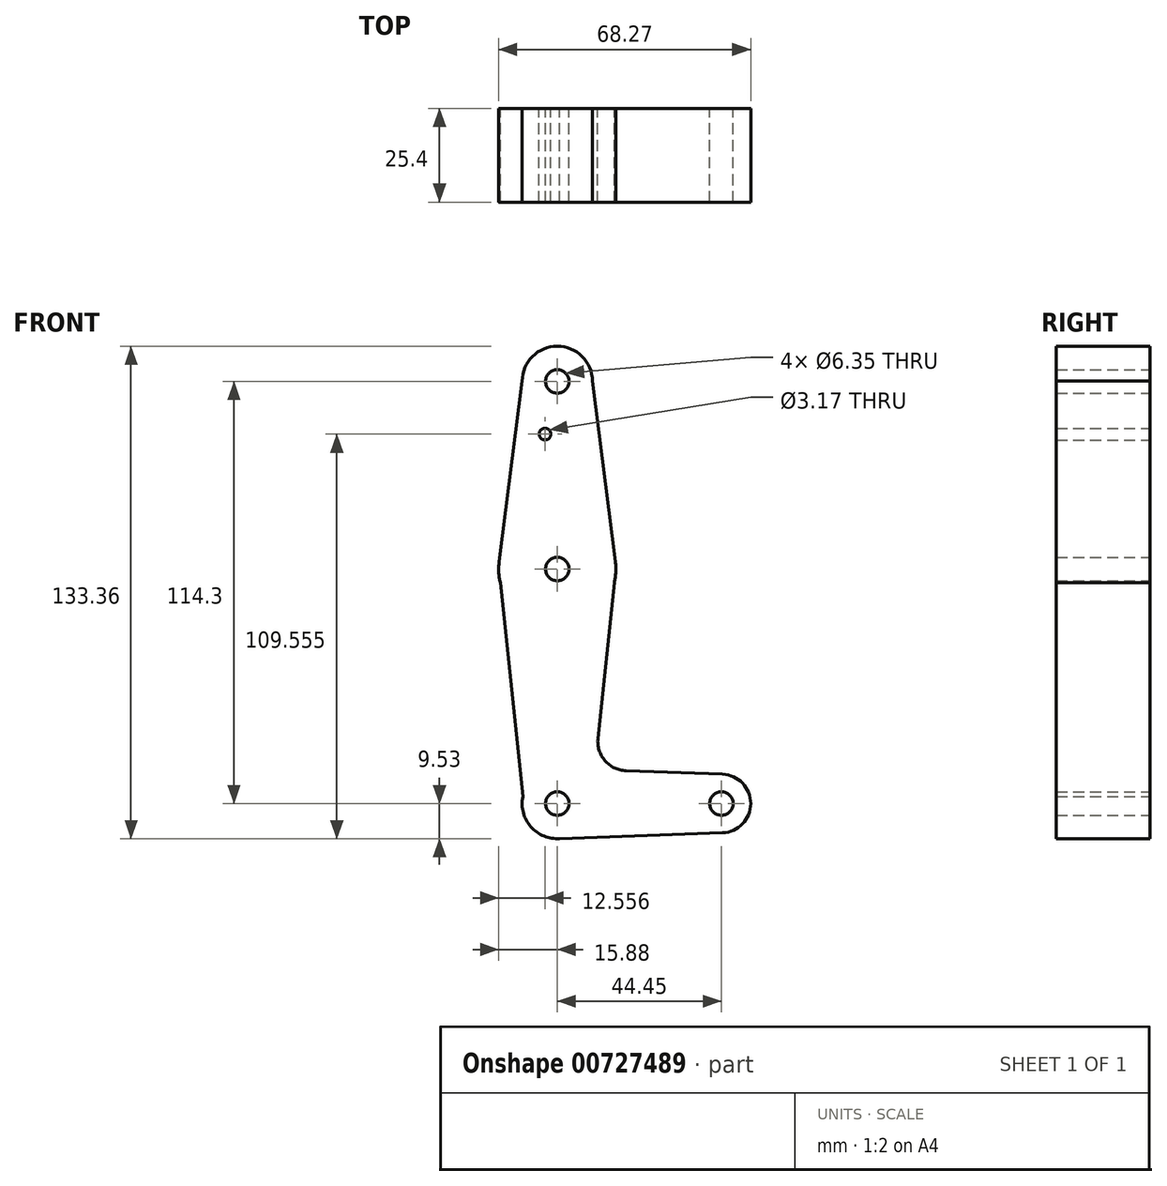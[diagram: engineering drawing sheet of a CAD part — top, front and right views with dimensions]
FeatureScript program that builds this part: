
annotation { "Feature Type Name" : "Feature", "Feature Type Description" : "" }
export const myFeature = defineFeature(function(context is Context, id is Id, definition is map)
    precondition{}
    {
        {
            var Q0;
            Q0=qCreatedBy(makeId("Front.planeOp"),FACE);
            var sketch = newSketch(context, id + "F0", { "sketchPlane" : qUnion([Q0])});
            skLineSegment(sketch, "E0", {"start": v(0, 0) * mm, "end": v(0, 114.3) * mm, "construction": true});
            skLineSegment(sketch, "E1", {"start": v(0, 0) * mm, "end": v(44.45, 0) * mm, "construction": true});
            skCircle(sketch, "E2", {"center": v(0, 114.3) * mm, "radius": 9.53 * mm});
            skCircle(sketch, "E3", {"center": v(0, 63.5) * mm, "radius": 15.88 * mm});
            skCircle(sketch, "E4", {"center": v(0, 0) * mm, "radius": 9.53 * mm});
            skCircle(sketch, "E5", {"center": v(44.45, 0) * mm, "radius": 7.94 * mm});
            skLineSegment(sketch, "E6", {"start": v(-9.52, 114.39) * mm, "end": v(-15.75, 65.5) * mm});
            skLineSegment(sketch, "E7", {"start": v(-15.44, 59.8) * mm, "end": v(-9.34, 1.84) * mm});
            skLineSegment(sketch, "E8", {"start": v(9.52, 114.39) * mm, "end": v(15.75, 65.5) * mm});
            skLineSegment(sketch, "E9", {"start": v(15.44, 59.8) * mm, "end": v(11, 17.64) * mm});
            skLineSegment(sketch, "E10", {"start": v(18.63, 8.86) * mm, "end": v(44.73, 7.93) * mm});
            skLineSegment(sketch, "E11", {"start": v(0, -9.53) * mm, "end": v(44.73, -7.93) * mm});
            skCircle(sketch, "E12", {"center": v(0, 114.3) * mm, "radius": 3.18 * mm});
            skCircle(sketch, "E13", {"center": v(0, 63.5) * mm, "radius": 3.18 * mm});
            skCircle(sketch, "E14", {"center": v(0, 0) * mm, "radius": 3.18 * mm});
            skCircle(sketch, "E15", {"center": v(44.45, 0) * mm, "radius": 3.18 * mm});
            skCircle(sketch, "E16", {"center": v(-3.32, 100.03) * mm, "radius": 1.59 * mm});
            skPoint(sketch, "E17.newPointA", {"position": v(9.34, 1.84) * mm});
            skArc(sketch, "E17.filletArc", {"start": v(11, 17.64) * mm, "mid": v(12.9, 11.6) * mm, "end": v(18.63, 8.86) * mm});
            skSolve(sketch);
        }
        {
            var Q0;
            Q0 = qSketchRegion(id + "F0", true);
            extrude(context, id + "F1", {"entities" : qUnion([Q0]), "depth" : 25.4 * mm, "offsetDistance" : 25.4 * mm});
        }
    });
